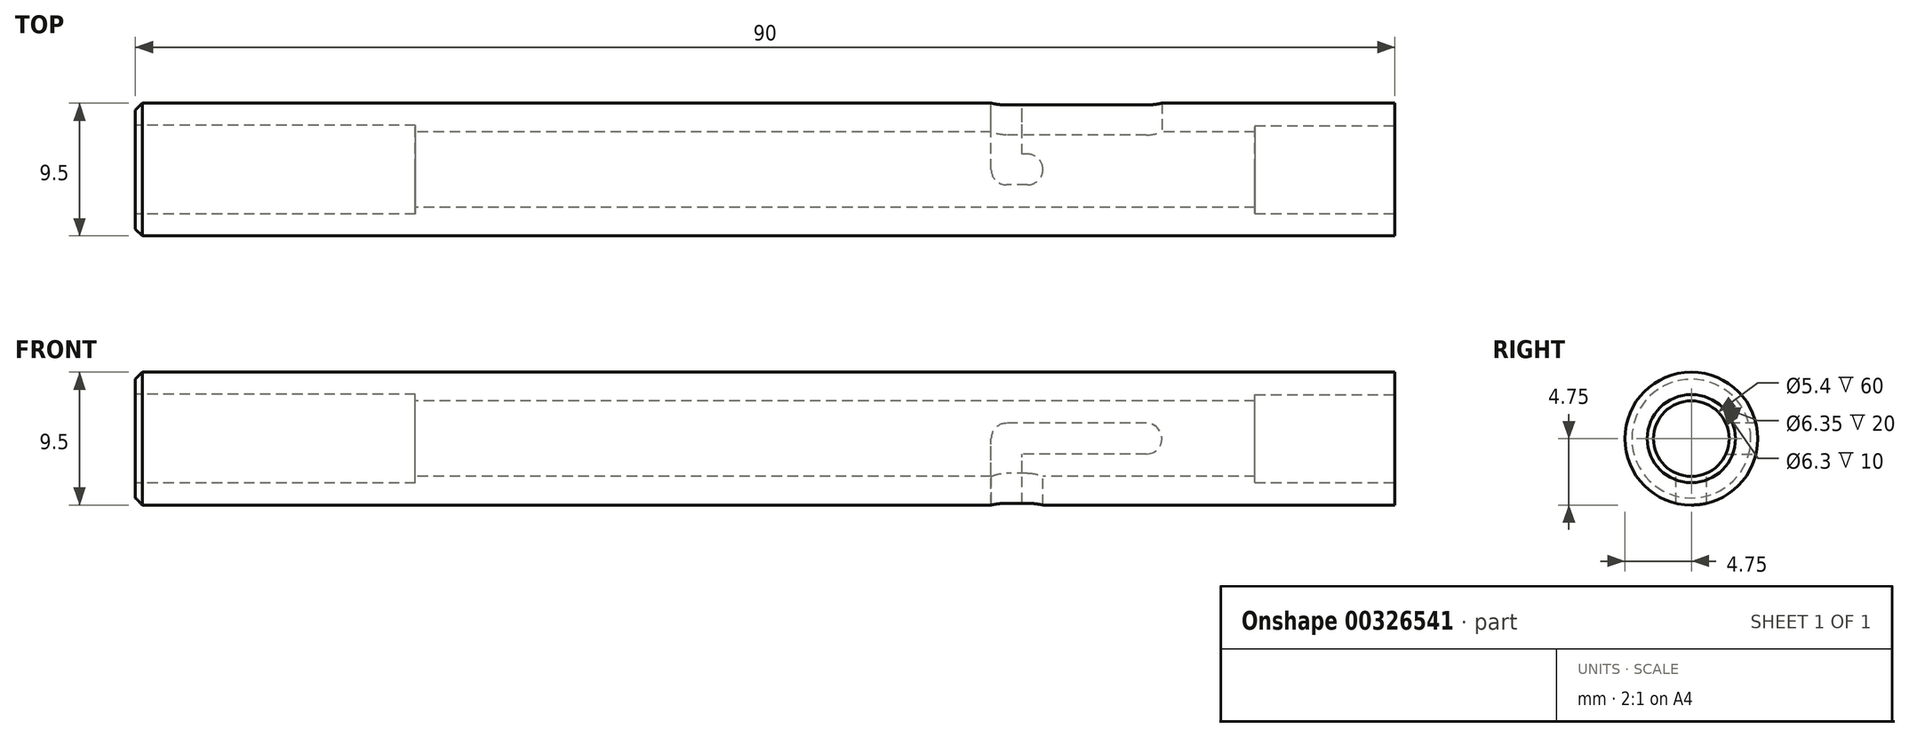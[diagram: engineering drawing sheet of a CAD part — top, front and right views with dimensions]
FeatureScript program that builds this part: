
annotation { "Feature Type Name" : "Feature", "Feature Type Description" : "" }
export const myFeature = defineFeature(function(context is Context, id is Id, definition is map)
    precondition{}
    {
        {
            var Q0;
            Q0=qCreatedBy(makeId("Right.planeOp"),FACE);
            var sketch = newSketch(context, id + "F0", { "sketchPlane" : qUnion([Q0])});
            skCircle(sketch, "E0", {"center": v(0, 0) * mm, "radius": 4.75 * mm});
            skSolve(sketch);
        }
        {
            var Q0;
            Q0=makeQuery(id+"F0.imprint","IMPRINT",FACE,{"disambiguationData":[TD([[makeQuery(id+"F0.imprint","IMPRINT",EDGE,{"derivedFrom":sQuery(id+"F0.wireOp",EDGE,"E0")}),1.0]])]});
            extrude(context, id + "F1", {"entities" : qUnion([Q0]), "depth" : 90 * mm});
        }
        {
            var Q0;
            Q0=qCreatedBy(makeId("Right.planeOp"),FACE);
            var sketch = newSketch(context, id + "F2", { "sketchPlane" : qUnion([Q0])});
            skCircle(sketch, "E1", {"center": v(0, 0) * mm, "radius": 2.7 * mm});
            skSolve(sketch);
        }
        {
            var Q0;
            Q0=makeQuery(id+"F2.imprint","IMPRINT",FACE,{"disambiguationData":[TD([[makeQuery(id+"F2.imprint","IMPRINT",EDGE,{"derivedFrom":sQuery(id+"F2.wireOp",EDGE,"E1")}),1.0]])]});
            extrude(context, id + "F3", {"entities" : qUnion([Q0]), "operationType" : NewBodyOperationType.REMOVE, "depth" : 100 * mm});
        }
        {
            var Q0;
            Q0=qCreatedBy(makeId("Right.planeOp"),FACE);
            var sketch = newSketch(context, id + "F4", { "sketchPlane" : qUnion([Q0])});
            skCircle(sketch, "E2", {"center": v(0, 0) * mm, "radius": 3.17 * mm});
            skSolve(sketch);
        }
        {
            var Q0;
            Q0 = qSketchRegion(id + "F4", true);
            extrude(context, id + "F5", {"entities" : qUnion([Q0]), "operationType" : NewBodyOperationType.REMOVE, "depth" : 20 * mm});
        }
        {
            var Q0;
            Q0=makeQuery(id+"F1.opExtrude","CAP_FACE",FACE,{"disambiguationData":[OSD([sQuery(id+"F0.wireOp",EDGE,"E0")])],"isStart":false});
            var sketch = newSketch(context, id + "F6", { "sketchPlane" : qUnion([Q0])});
            skCircle(sketch, "E3", {"center": v(0, 0) * mm, "radius": 3.15 * mm});
            skSolve(sketch);
        }
        {
            var Q0;
            Q0=makeQuery(id+"F6.imprint","IMPRINT",FACE,{"disambiguationData":[TD([[makeQuery(id+"F6.imprint","IMPRINT",EDGE,{"derivedFrom":sQuery(id+"F6.wireOp",EDGE,"E3")}),1.0]])]});
            extrude(context, id + "F7", {"entities" : qUnion([Q0]), "operationType" : NewBodyOperationType.REMOVE, "oppositeDirection" : true, "depth" : 10 * mm});
        }
        {
            var Q0;
            Q0=qCreatedBy(makeId("Front.planeOp"),FACE);
            var sketch = newSketch(context, id + "F8", { "sketchPlane" : qUnion([Q0])});
            skLineSegment(sketch, "E4", {"start": v(72.25, 0) * mm, "end": v(62.25, 0) * mm});
            skArc(sketch, "E5.0.startCap", {"start": v(72.25, 1.1) * mm, "mid": v(73.35, 0) * mm, "end": v(72.25, -1.1) * mm});
            skArc(sketch, "E5.0.endCap", {"start": v(62.25, -1.1) * mm, "mid": v(61.15, 0) * mm, "end": v(62.25, 1.1) * mm});
            skLineSegment(sketch, "E5.0.left", {"start": v(72.25, -1.1) * mm, "end": v(62.25, -1.1) * mm});
            skLineSegment(sketch, "E5.0.right", {"start": v(72.25, 1.1) * mm, "end": v(62.25, 1.1) * mm});
            skSolve(sketch);
        }
        {
            var Q0;
            Q0 = qSketchRegion(id + "F8", true);
            extrude(context, id + "F9", {"entities" : qUnion([Q0]), "operationType" : NewBodyOperationType.REMOVE, "oppositeDirection" : true, "depth" : 25 * mm});
        }
        {
            var Q0;
            Q0=qCreatedBy(makeId("Top.planeOp"),FACE);
            var sketch = newSketch(context, id + "F10", { "sketchPlane" : qUnion([Q0])});
            skLineSegment(sketch, "E6", {"start": v(62.25, 0) * mm, "end": v(63.75, 0) * mm});
            skArc(sketch, "E7.0.startCap", {"start": v(62.25, -1.1) * mm, "mid": v(61.15, 0) * mm, "end": v(62.25, 1.1) * mm});
            skArc(sketch, "E7.0.endCap", {"start": v(63.75, 1.1) * mm, "mid": v(64.85, 0) * mm, "end": v(63.75, -1.1) * mm});
            skLineSegment(sketch, "E7.0.left", {"start": v(62.25, 1.1) * mm, "end": v(63.75, 1.1) * mm});
            skLineSegment(sketch, "E7.0.right", {"start": v(62.25, -1.1) * mm, "end": v(63.75, -1.1) * mm});
            skSolve(sketch);
        }
        {
            var Q0;
            Q0 = qSketchRegion(id + "F10", true);
            extrude(context, id + "F11", {"entities" : qUnion([Q0]), "operationType" : NewBodyOperationType.REMOVE, "oppositeDirection" : true, "depth" : 25 * mm});
        }
        {
            var Q0;
            Q0=qCreatedBy(makeId("Right.planeOp"),FACE);
            cPlane(context, id + "F12", {"entities" : qUnion([Q0]), "cplaneType" : CPlaneType.OFFSET, "offset" : 62.25 * mm, "width" : 150 * mm, "height" : 150 * mm});
        }
        {
            var Q0;
            Q0=qCreatedBy(id+"F12.planeOp",FACE);
            var sketch = newSketch(context, id + "F13", { "sketchPlane" : qUnion([Q0])});
            skArc(sketch, "E8", {"start": v(0, -11.8) * mm, "mid": v(8.34, -8.34) * mm, "end": v(11.8, 0) * mm});
            skLineSegment(sketch, "E9", {"start": v(0, 0) * mm, "end": v(11.8, 0) * mm});
            skLineSegment(sketch, "E10", {"start": v(0, 0) * mm, "end": v(0, -11.8) * mm});
            skSolve(sketch);
        }
        {
            var Q0;
            Q0 = qSketchRegion(id + "F13", true);
            extrude(context, id + "F14", {"entities" : qUnion([Q0]), "operationType" : NewBodyOperationType.REMOVE, "oppositeDirection" : true, "depth" : 2.2 * mm, "symmetric" : true});
        }
        {
            var Q0;
            Q0=makeQuery(id+"F1.opExtrude","CAP_EDGE",EDGE,{"disambiguationData":[OSD([sQuery(id+"F0.wireOp",EDGE,"E0")])],"isStart":true});
            chamfer(context, id + "F15", {"entities" : qUnion([Q0]), "width" : .5 * mm, "tangentPropagation" : true});
        }
    });
